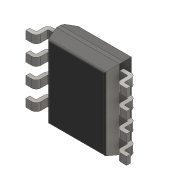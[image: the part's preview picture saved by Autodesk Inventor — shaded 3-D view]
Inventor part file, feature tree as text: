
AUTODESK INVENTOR PART (.ipt)
format: ipt  version: 2016 (Build 200138000, 138)  size: 317,440 bytes
history: native  units: mm
features: chamfer x8, extrude x6, sketch x6, fillet x3, mirror x1, projected_geometry x1
ambient origin geometry x8: Origin, YZ Plane, XZ Plane, XY Plane, X Axis, Y Axis, Z Axis, Center Point
bodies: Solid1 (feature_tree)
feature tree (25):
  extrude  "Extrusion1"  Depth=5.0mm
  chamfer  "Chamfer1"  Distance=1.75mm
  chamfer  "Chamfer2"  Distance=0.5mm Angle=45.0deg
  chamfer  "Chamfer3"  Distance=0.2mm Angle=75.0deg
  chamfer  "Chamfer4"  Distance=0.2mm Angle=75.0deg
  chamfer  "Chamfer5"  Distance=0.2mm Angle=75.0deg
  chamfer  "Chamfer6"  Distance=0.2mm Angle=75.0deg
  chamfer  "Chamfer7"  Distance=0.2mm Angle=75.0deg
  chamfer  "Chamfer8"  Distance=0.2mm Angle=75.0deg
  fillet  "Fillet1"  Radius=0.1mm
  extrude  "Extrusion2"  Depth=0.3mm TaperAngle=0.0deg
  extrude  "Extrusion3"  Depth=0.1mm TaperAngle=0.0deg
  extrude  "Extrusion4"  Depth=0.25mm
  extrude  "Extrusion5"  Depth=0.41mm
  fillet  "Fillet2"  Radius=0.25mm
  fillet  "Fillet3"  Radius=0.1mm
  extrude  "Extrusion6"  Depth=0.3mm
  mirror  "Mirror1"
  sketch  "Sketch1"  dims[d0=4.0mm d1=5.0mm d2=1.75mm d3=0.0mm d4=0.5mm d5=2.0mm d6=45.0deg d7=0.2mm d8=2.0mm d9=75.0deg d10=0.2mm d11=2.0mm d12=75.0deg d13=0.2mm d14=2.0mm d15=75.0deg d16=0.2mm d17=2.0mm d18=75.0deg d19=0.2mm d20=2.0mm d21=75.0deg d22=0.2mm d23=2.0mm d24=75.0deg]
  sketch  "Sketch2"  dims[d25=0.2mm d26=2.0mm d27=75.0deg d28=0.1mm]
  sketch  "Sketch3"  dims[d29=2.8mm d30=0.3mm d31=0.0mm]
  sketch  "Sketch4"  dims[d32=0.1mm d33=0.0mm d34=0.1mm d35=0.0mm]
  sketch  "Sketch5"  dims[d36=1.2mm d37=0.25mm]
  projected_geometry  "Projected Loop1"
  sketch  "Sketch6"  dims[d38=0.25mm d39=0.41mm d40=0.25mm d41=0.1mm d42=0.0mm d43=0.3mm d44=0.066mm d47=2.12mm d48=0.5mm d49=0.745mm d50=0.5mm d51=0.745mm d52=0.5mm d53=0.745mm d54=0.5mm d55=0.0mm d56=0.1mm d57=0.0mm]
